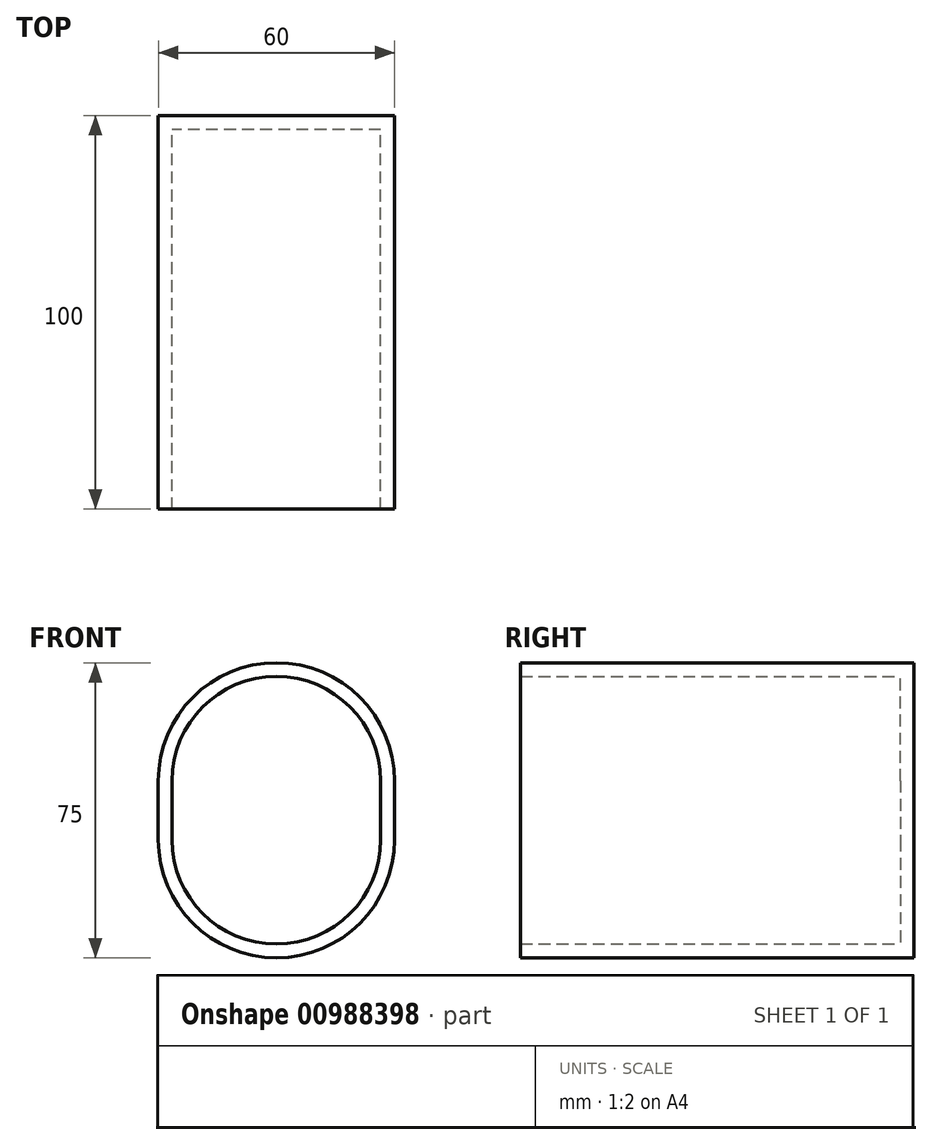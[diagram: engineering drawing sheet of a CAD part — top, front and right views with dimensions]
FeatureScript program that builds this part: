
annotation { "Feature Type Name" : "Feature", "Feature Type Description" : "" }
export const myFeature = defineFeature(function(context is Context, id is Id, definition is map)
    precondition{}
    {
        {
            var Q0;
            Q0=qCreatedBy(makeId("Front.planeOp"),FACE);
            var sketch = newSketch(context, id + "F0", { "sketchPlane" : qUnion([Q0])});
            skArc(sketch, "E0", {"start": v(35.75, 0) * mm, "mid": v(5.75, 30) * mm, "end": v(-24.25, 0) * mm});
            skLineSegment(sketch, "E1", {"start": v(-24.25, 0) * mm, "end": v(-24.25, -15) * mm});
            skLineSegment(sketch, "E2", {"start": v(35.75, 0) * mm, "end": v(35.75, -15) * mm});
            skArc(sketch, "E3", {"start": v(-24.25, -15) * mm, "mid": v(5.75, -45) * mm, "end": v(35.75, -15) * mm});
            skSolve(sketch);
        }
        {
            var Q0;
            Q0=makeQuery(id+"F0.imprint","IMPRINT",FACE,{"disambiguationData":[TD([[makeQuery(id+"F0.imprint","IMPRINT",EDGE,{"derivedFrom":sQuery(id+"F0.wireOp",EDGE,"E0")}),1.0]])]});
            extrude(context, id + "F1", {"entities" : qUnion([Q0]), "depth" : 100 * mm, "offsetDistance" : 25 * mm});
        }
        {
            var Q0;
            Q0=makeQuery(id+"F1.opExtrude","CAP_FACE",FACE,{"disambiguationData":[OSD([sQuery(id+"F0.wireOp",EDGE,"E0"),sQuery(id+"F0.wireOp",EDGE,"E1"),sQuery(id+"F0.wireOp",EDGE,"E2"),sQuery(id+"F0.wireOp",EDGE,"E3")])],"isStart":false});
            shell(context, id + "F2", {"entities" : qUnion([Q0]), "thickness" : 3.5 * mm});
        }
    });
